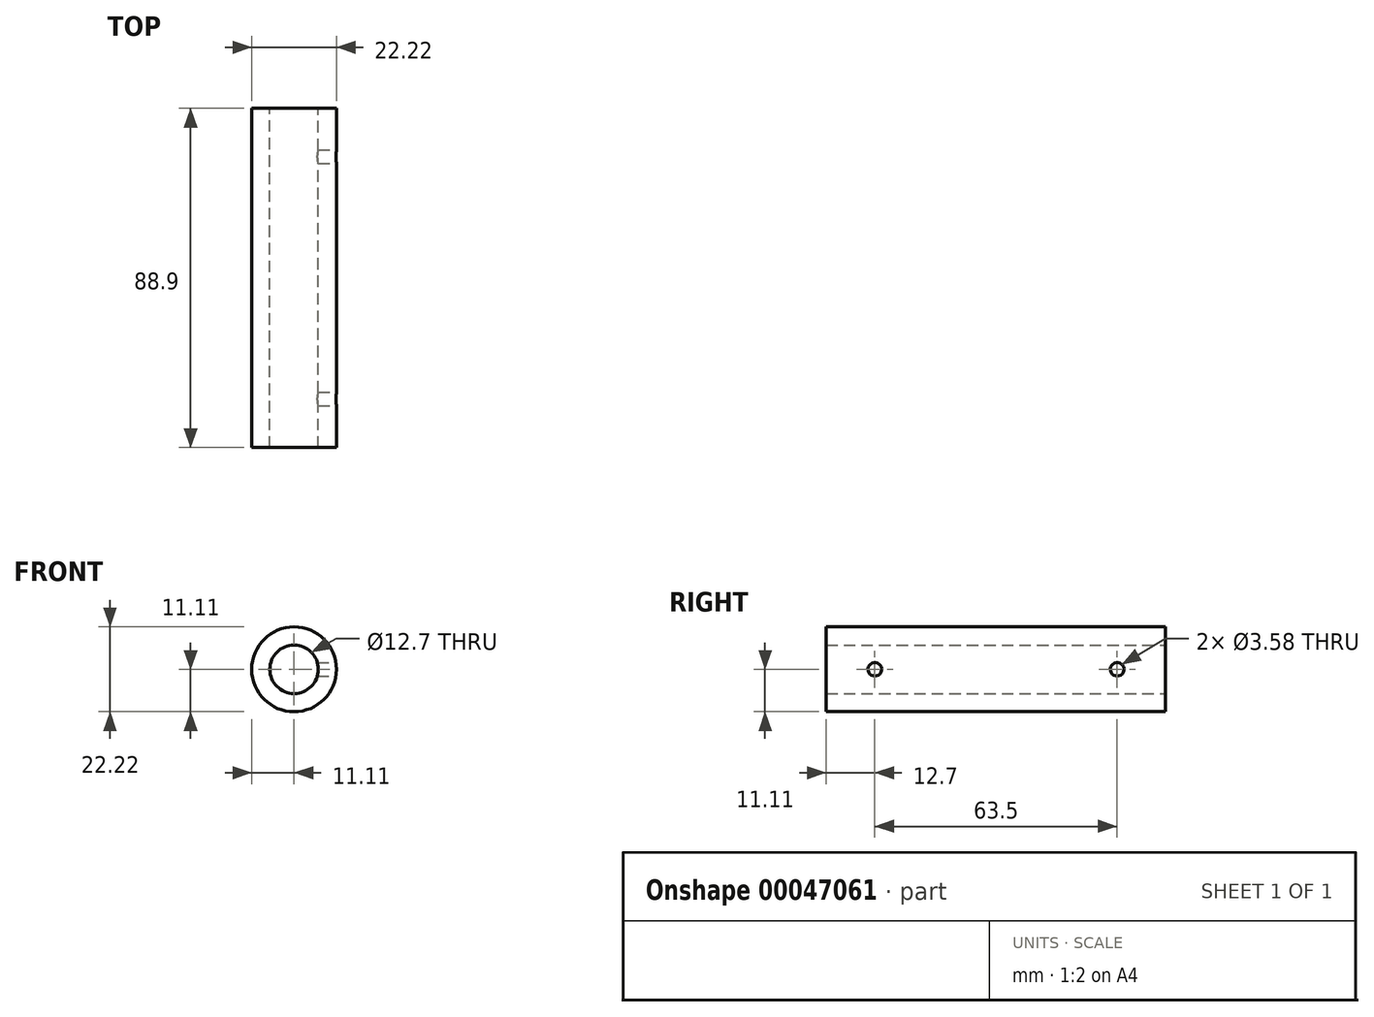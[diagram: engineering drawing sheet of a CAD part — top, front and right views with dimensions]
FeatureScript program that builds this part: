
annotation { "Feature Type Name" : "Feature", "Feature Type Description" : "" }
export const myFeature = defineFeature(function(context is Context, id is Id, definition is map)
    precondition{}
    {
        {
            var Q0;
            Q0=qCreatedBy(makeId("Front.planeOp"),FACE);
            var sketch = newSketch(context, id + "F0", { "sketchPlane" : qUnion([Q0])});
            skCircle(sketch, "E0", {"center": v(0, 0) * mm, "radius": 11.11 * mm});
            skCircle(sketch, "E1", {"center": v(0, 0) * mm, "radius": 6.35 * mm});
            skSolve(sketch);
        }
        {
            var Q0;
            Q0=makeQuery(id+"F0.imprint","IMPRINT",FACE,{"disambiguationData":[TD([[makeQuery(id+"F0.imprint","IMPRINT",EDGE,{"derivedFrom":sQuery(id+"F0.wireOp",EDGE,"E0")}),1.0]])]});
            extrude(context, id + "F1", {"entities" : qUnion([Q0]), "endBound" : BoundingType.SYMMETRIC, "depth" : 88.9 * mm});
        }
        {
            var Q0;
            Q0=qCreatedBy(makeId("Right.planeOp"),FACE);
            cPlane(context, id + "F2", {"entities" : qUnion([Q0]), "cplaneType" : CPlaneType.OFFSET, "offset" : 11.1 * mm, "width" : 152.4 * mm, "height" : 152.4 * mm});
        }
        {
            var Q0;
            Q0=qCreatedBy(id+"F2.planeOp",FACE);
            var sketch = newSketch(context, id + "F3", { "sketchPlane" : qUnion([Q0])});
            skCircle(sketch, "E2", {"center": v(-31.75, 0) * mm, "radius": 1.8 * mm});
            skCircle(sketch, "E3.MirrorC", {"center": v(31.75, 0) * mm, "radius": 1.8 * mm});
            skSolve(sketch);
        }
        {
            var Q0;
            Q0 = qSketchRegion(id + "F3", true);
            var Q1;
            Q1=makeQuery(id+"F1.opExtrude","SWEPT_FACE",FACE,{"disambiguationData":[OSD([sQuery(id+"F0.wireOp",EDGE,"E1")])]});
            extrude(context, id + "F4", {"entities" : qUnion([Q0]), "operationType" : NewBodyOperationType.REMOVE, "endBound" : BoundingType.UP_TO_SURFACE, "oppositeDirection" : true, "endBoundEntityFace" : qUnion([Q1]), "depth" : 25.4 * mm});
        }
    });
